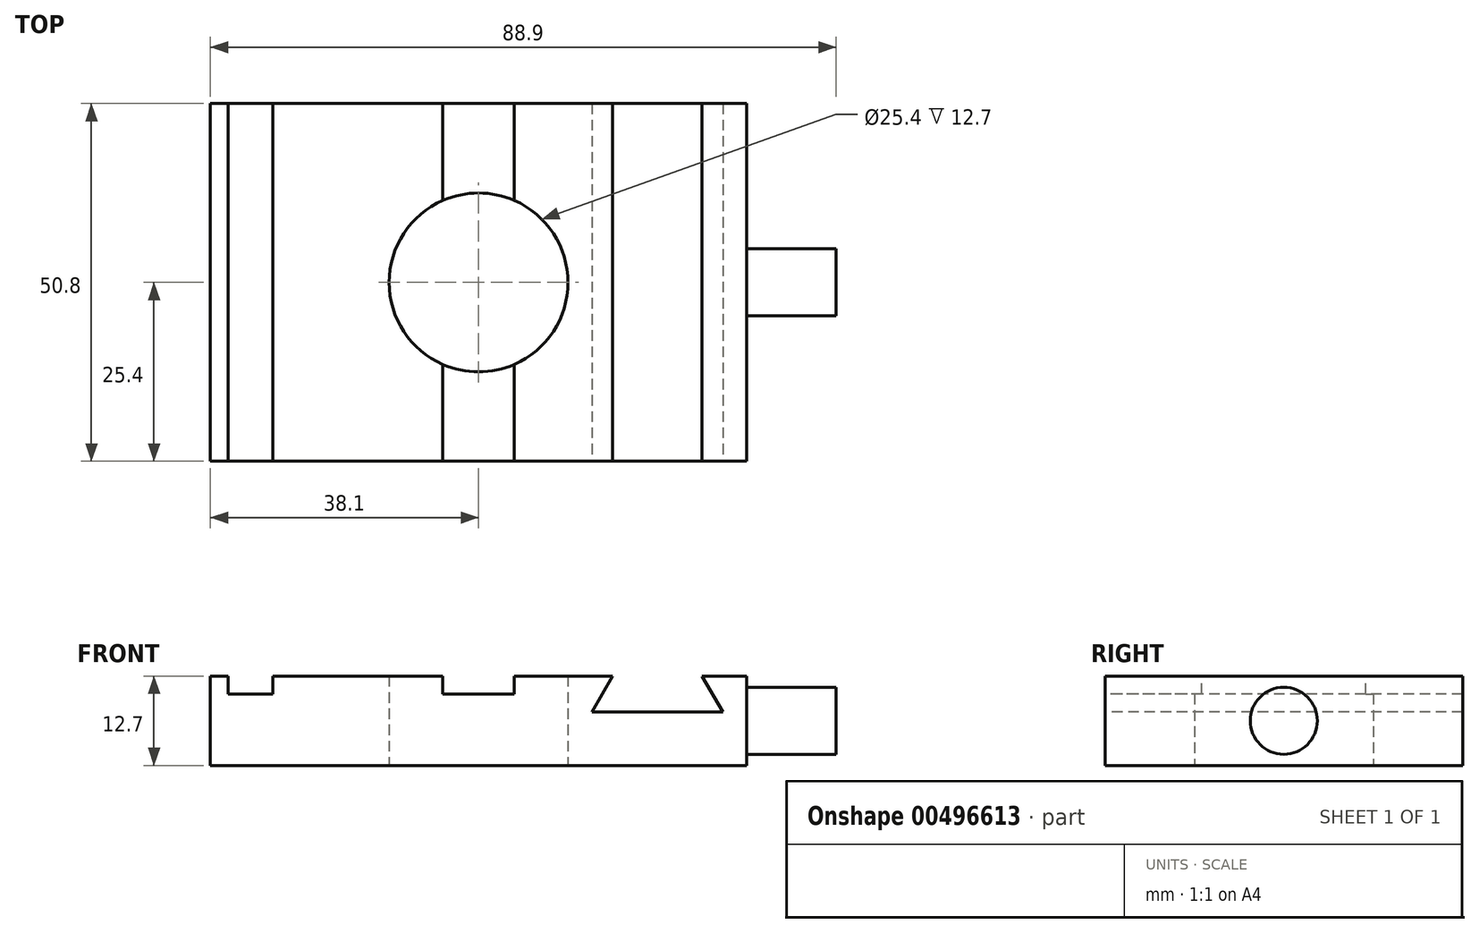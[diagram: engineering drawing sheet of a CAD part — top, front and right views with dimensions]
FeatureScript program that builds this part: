
annotation { "Feature Type Name" : "Feature", "Feature Type Description" : "" }
export const myFeature = defineFeature(function(context is Context, id is Id, definition is map)
    precondition{}
    {
        {
            var Q0;
            Q0=qCreatedBy(makeId("Top.planeOp"),FACE);
            var sketch = newSketch(context, id + "F0", { "sketchPlane" : qUnion([Q0])});
            skLineSegment(sketch, "E0.bottom", {"start": v(38.1, 25.4) * mm, "end": v(-38.1, 25.4) * mm});
            skLineSegment(sketch, "E0.top", {"start": v(38.1, -25.4) * mm, "end": v(-38.1, -25.4) * mm});
            skLineSegment(sketch, "E0.left", {"start": v(38.1, 25.4) * mm, "end": v(38.1, -25.4) * mm});
            skLineSegment(sketch, "E0.right", {"start": v(-38.1, 25.4) * mm, "end": v(-38.1, -25.4) * mm});
            skPoint(sketch, "E0.middle", {"position": v(0, 0) * mm});
            skCircle(sketch, "E1", {"center": v(0, 0) * mm, "radius": 12.7 * mm});
            skSolve(sketch);
        }
        {
            var Q0;
            Q0 = qSketchRegion(id + "F0", true);
            extrude(context, id + "F1", {"entities" : qUnion([Q0]), "depth" : 12.7 * mm, "offsetDistance" : 25.4 * mm});
        }
        {
            var Q0;
            Q0=makeQuery(id+"F1.opExtrude","CAP_FACE",FACE,{"disambiguationData":[OSD([sQuery(id+"F0.wireOp",EDGE,"E0.bottom"),sQuery(id+"F0.wireOp",EDGE,"E0.top"),sQuery(id+"F0.wireOp",EDGE,"E0.left"),sQuery(id+"F0.wireOp",EDGE,"E0.right"),sQuery(id+"F0.wireOp",EDGE,"E1")])],"isStart":false});
            var sketch = newSketch(context, id + "F2", { "sketchPlane" : qUnion([Q0])});
            skLineSegment(sketch, "E2.bottom", {"start": v(-35.56, 25.4) * mm, "end": v(-29.21, 25.4) * mm});
            skLineSegment(sketch, "E2.top", {"start": v(-35.56, -25.4) * mm, "end": v(-29.21, -25.4) * mm});
            skLineSegment(sketch, "E2.left", {"start": v(-35.56, 25.4) * mm, "end": v(-35.56, -25.4) * mm});
            skLineSegment(sketch, "E2.right", {"start": v(-29.21, 25.4) * mm, "end": v(-29.21, -25.4) * mm});
            skLineSegment(sketch, "E3.bottom", {"start": v(-5.08, 25.4) * mm, "end": v(5.08, 25.4) * mm});
            skLineSegment(sketch, "E3.top", {"start": v(-5.08, -25.4) * mm, "end": v(5.08, -25.4) * mm});
            skLineSegment(sketch, "E3.left", {"start": v(-5.08, 25.4) * mm, "end": v(-5.08, -25.4) * mm});
            skLineSegment(sketch, "E3.right", {"start": v(5.08, 25.4) * mm, "end": v(5.08, -25.4) * mm});
            skPoint(sketch, "E4", {"position": v(0, 0) * mm});
            skLineSegment(sketch, "E5", {"start": v(0, 25.4) * mm, "end": v(0, -25.4) * mm, "construction": true});
            skSolve(sketch);
        }
        {
            var Q0;
            Q0=makeQuery(id+"F2.imprint","IMPRINT",FACE,{"disambiguationData":[TD([[makeQuery(id+"F2.imprint","IMPRINT",EDGE,{"derivedFrom":sQuery(id+"F2.wireOp",EDGE,"E2.bottom")}),1.0]])]});
            var Q1;
            {var subQ0=sQuery(id+"F2.wireOp",EDGE,"E3.bottom");Q1=makeQuery(id+"F2.imprint","IMPRINT",FACE,{"disambiguationData":[TD([[makeQuery(id+"F2.imprint","IMPRINT",EDGE,{"derivedFrom":subQ0}),1.0]])]});}
            var Q2;
            {var subQ0=sQuery(id+"F2.wireOp",EDGE,"E3.top");Q2=makeQuery(id+"F2.imprint","IMPRINT",FACE,{"disambiguationData":[TD([[makeQuery(id+"F2.imprint","IMPRINT",EDGE,{"derivedFrom":subQ0}),-1.0]])]});}
            extrude(context, id + "F3", {"entities" : qUnion([Q0, Q1, Q2]), "operationType" : NewBodyOperationType.REMOVE, "oppositeDirection" : true, "depth" : 2.54 * mm, "offsetDistance" : 25.4 * mm});
        }
        {
            var Q0;
            Q0=makeQuery(id+"F1.opExtrude","SWEPT_FACE",FACE,{"disambiguationData":[OSD([sQuery(id+"F0.wireOp",EDGE,"E0.top")])]});
            var sketch = newSketch(context, id + "F4", { "sketchPlane" : qUnion([Q0])});
            skLineSegment(sketch, "E6", {"start": v(19.05, 12.7) * mm, "end": v(16.12, 7.62) * mm});
            skLineSegment(sketch, "E7", {"start": v(16.12, 7.62) * mm, "end": v(34.68, 7.62) * mm});
            skLineSegment(sketch, "E8", {"start": v(34.68, 7.62) * mm, "end": v(31.75, 12.7) * mm});
            skLineSegment(sketch, "E9", {"start": v(31.75, 12.7) * mm, "end": v(19.05, 12.7) * mm});
            skLineSegment(sketch, "E10", {"start": v(25.4, 7.62) * mm, "end": v(25.4, 12.7) * mm, "construction": true});
            skSolve(sketch);
        }
        {
            var Q0;
            Q0 = qSketchRegion(id + "F4", true);
            extrude(context, id + "F5", {"entities" : qUnion([Q0]), "operationType" : NewBodyOperationType.REMOVE, "endBound" : BoundingType.UP_TO_NEXT, "oppositeDirection" : true, "depth" : 25.4 * mm, "offsetDistance" : 25.4 * mm});
        }
        {
            var Q0;
            Q0=makeQuery(id+"F1.opExtrude","SWEPT_FACE",FACE,{"disambiguationData":[OSD([sQuery(id+"F0.wireOp",EDGE,"E0.left")])]});
            var sketch = newSketch(context, id + "F6", { "sketchPlane" : qUnion([Q0])});
            skCircle(sketch, "E11", {"center": v(0, 6.35) * mm, "radius": 4.76 * mm});
            skPoint(sketch, "E11.centerSnap0", {"position": v(-25.4, 6.35) * mm});
            skSolve(sketch);
        }
        {
            var Q0;
            Q0 = qSketchRegion(id + "F6", true);
            extrude(context, id + "F7", {"entities" : qUnion([Q0]), "operationType" : NewBodyOperationType.ADD, "depth" : 12.7 * mm, "offsetDistance" : 25.4 * mm});
        }
    });
